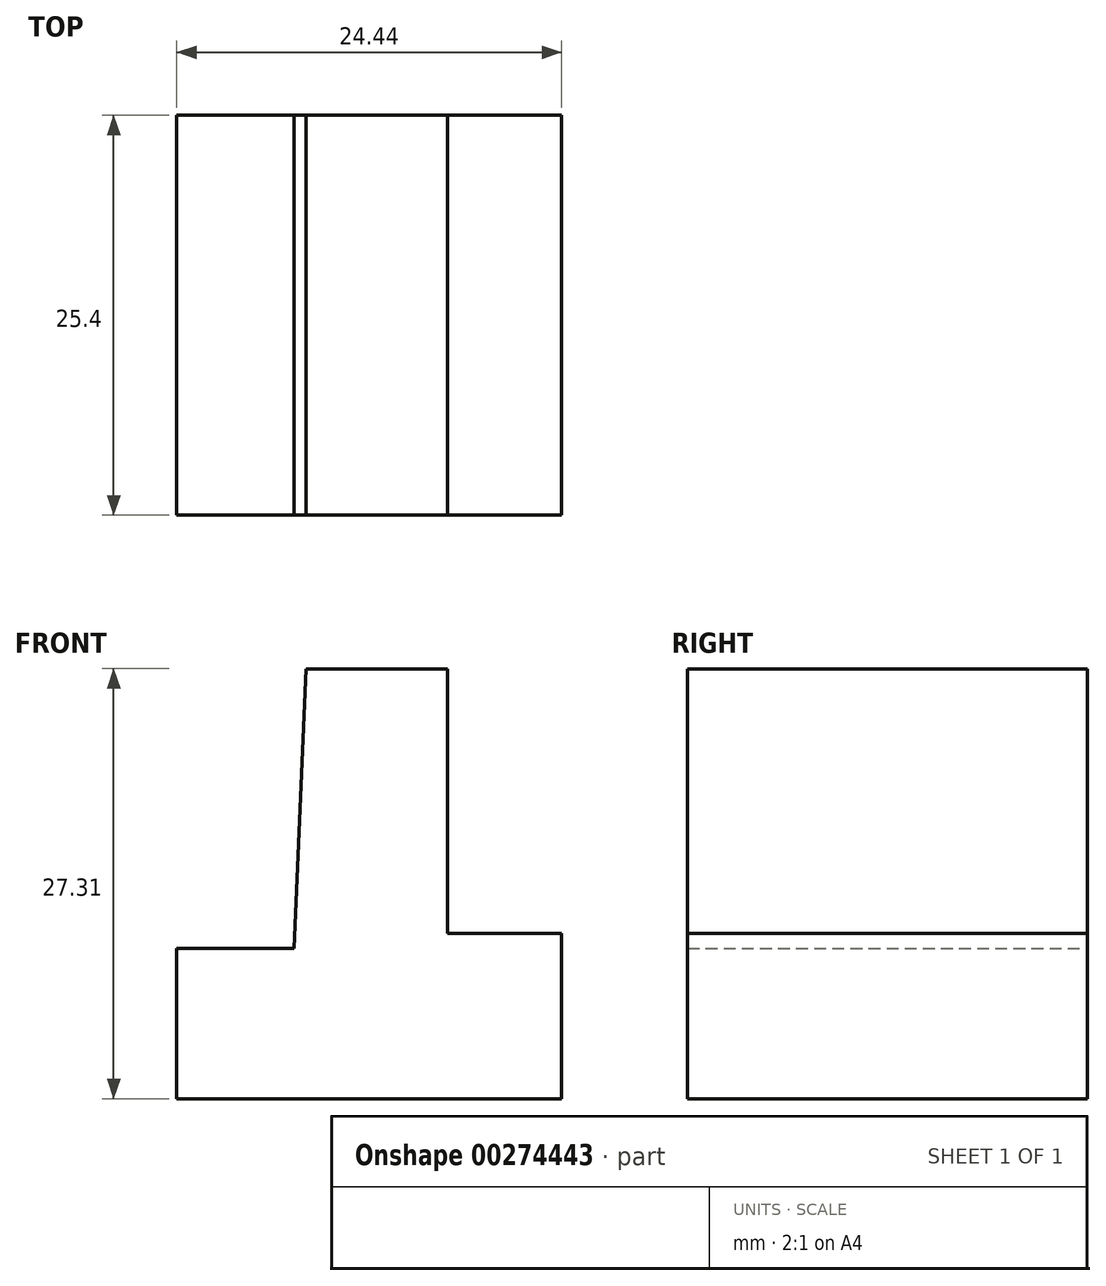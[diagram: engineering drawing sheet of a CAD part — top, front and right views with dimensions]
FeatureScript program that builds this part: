
annotation { "Feature Type Name" : "Feature", "Feature Type Description" : "" }
export const myFeature = defineFeature(function(context is Context, id is Id, definition is map)
    precondition{}
    {
        {
            var Q0;
            Q0=qCreatedBy(makeId("Front.planeOp"),FACE);
            var sketch = newSketch(context, id + "F0", { "sketchPlane" : qUnion([Q0])});
            skLineSegment(sketch, "E0", {"start": v(-49.46, 29.4) * mm, "end": v(-40.48, 29.4) * mm});
            skLineSegment(sketch, "E1", {"start": v(-40.48, 29.4) * mm, "end": v(-40.48, 12.6) * mm});
            skLineSegment(sketch, "E2", {"start": v(-40.48, 12.6) * mm, "end": v(-33.23, 12.6) * mm});
            skLineSegment(sketch, "E3", {"start": v(-33.23, 12.6) * mm, "end": v(-33.23, 2.1) * mm});
            skLineSegment(sketch, "E4", {"start": v(-33.23, 2.1) * mm, "end": v(-57.67, 2.1) * mm});
            skLineSegment(sketch, "E5", {"start": v(-57.67, 2.1) * mm, "end": v(-57.67, 11.65) * mm});
            skLineSegment(sketch, "E6", {"start": v(-57.67, 11.65) * mm, "end": v(-50.22, 11.65) * mm});
            skLineSegment(sketch, "E7", {"start": v(-50.22, 11.65) * mm, "end": v(-49.46, 29.4) * mm});
            skSolve(sketch);
        }
        {
            var Q0;
            Q0 = qSketchRegion(id + "F0", true);
            extrude(context, id + "F1", {"entities" : qUnion([Q0]), "depth" : 25.4 * mm});
        }
    });
